AUTODESK INVENTOR PART (.ipt)
format: ipt  version: 2023 (Build 270158030, 158C)  size: 236,032 bytes
history: native  units: mm
features: other x10, sketch x4, plane x1, extrude x1
ambient origin geometry x8: Origin, YZ Plane, XZ Plane, XY Plane, X Axis, Y Axis, Z Axis, Center Point
bodies: Body1 (feature_tree)
feature tree (16):
  other  "mode-select-layout"
  plane  "Work Plane1"
  extrude  "Extrusion1"  Depth=22.0mm
  other  "Decal1"
  other  "Decal2"
  other  "Decal3"
  sketch  "Sketch1"  dims[d0=22.0mm d1=22.0mm]
  sketch  "Sketch5"  dims[d2=90.0mm]
  other  "Image3"
  sketch  "Sketch6"  dims[d7=29.0mm]
  other  "Image6"
  sketch  "Sketch7"  dims[d8=16.0mm d9=16.0mm d10=20.0mm d11=20.0mm d12=30.0mm d14=40.0mm d17=37.0mm d18=20.0mm d19=10.0mm d20=10.0mm d21=30.0mm d22=35.0mm d24=1.0mm d25=0.0mm d26=39.051248mm d28=4.3mm d29=4.8mm d30=10.0mm d31=10.0mm d124=10.813395mm d125=9.186605mm d126=12.0mm d130=1.6mm d131=1.6mm d132=2.0mm]
  other  "Image7"
  other  "<userpath>\Documents\0004-inventor\Inventor_Projects\electronics-enclosure\enclosure.iam"
  other  "enclosure.iam"
  other  "door:1"
